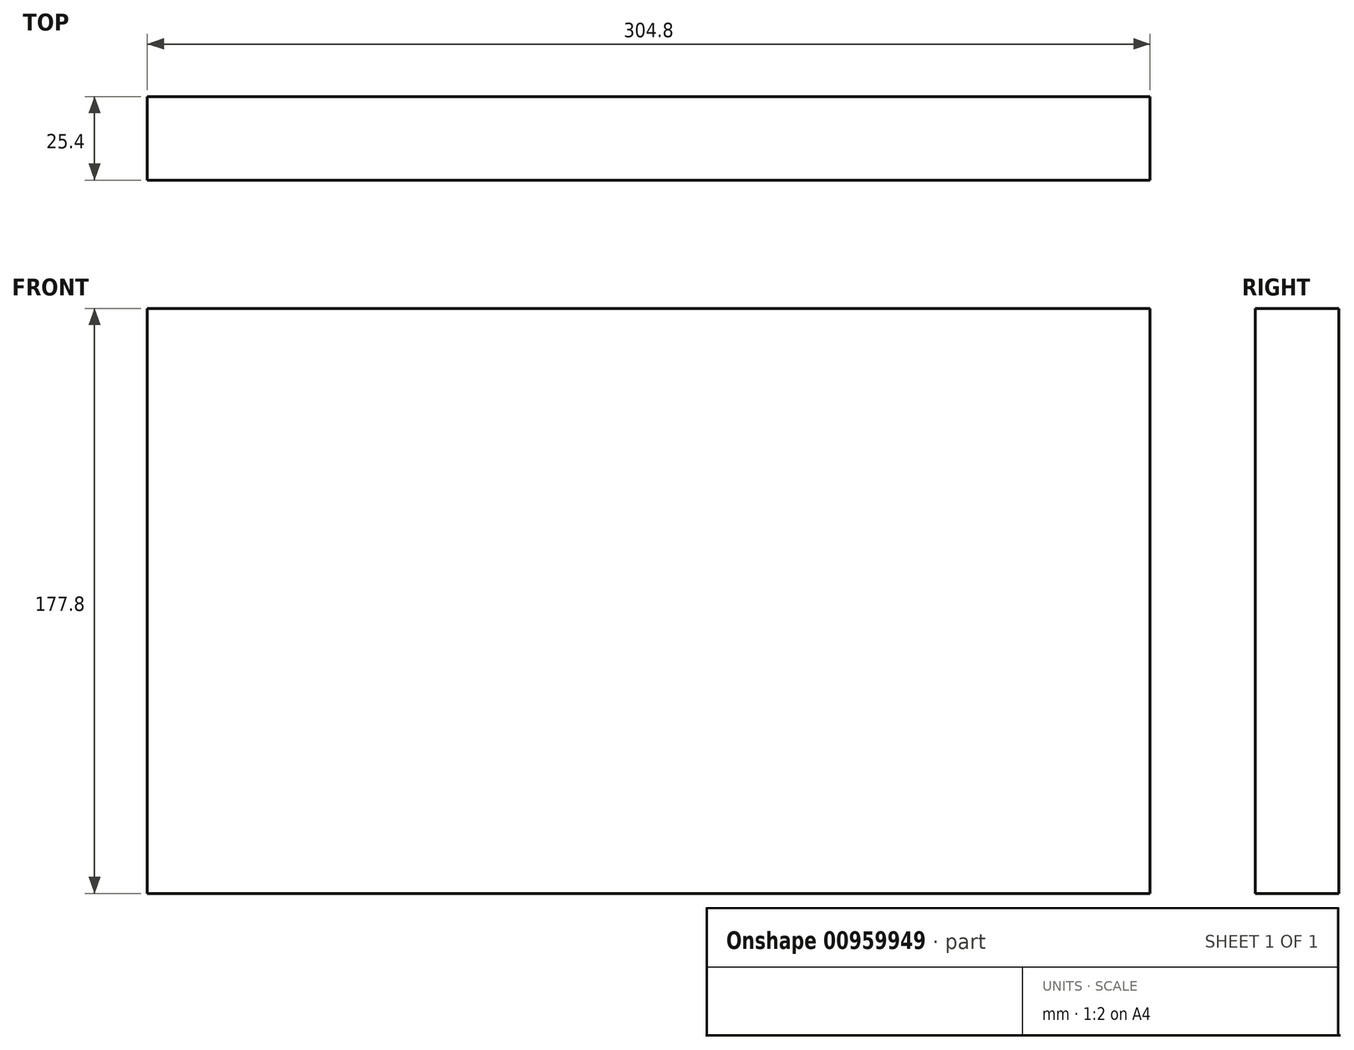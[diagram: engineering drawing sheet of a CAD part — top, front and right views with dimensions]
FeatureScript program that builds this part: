
annotation { "Feature Type Name" : "Feature", "Feature Type Description" : "" }
export const myFeature = defineFeature(function(context is Context, id is Id, definition is map)
    precondition{}
    {
        {
            var Q0;
            Q0=qCreatedBy(makeId("Front.planeOp"),FACE);
            var sketch = newSketch(context, id + "F0", { "sketchPlane" : qUnion([Q0])});
            skLineSegment(sketch, "E0.bottom", {"start": v(-88.9, -88.9) * mm, "end": v(88.9, -88.9) * mm});
            skLineSegment(sketch, "E0.top", {"start": v(-88.9, 88.9) * mm, "end": v(88.9, 88.9) * mm});
            skLineSegment(sketch, "E0.left", {"start": v(-88.9, -88.9) * mm, "end": v(-88.9, 88.9) * mm});
            skLineSegment(sketch, "E0.right", {"start": v(88.9, -88.9) * mm, "end": v(88.9, 88.9) * mm});
            skPoint(sketch, "E0.middle", {"position": v(0, 0) * mm});
            skLineSegment(sketch, "E1", {"start": v(-88.9, 88.9) * mm, "end": v(-215.9, 88.9) * mm});
            skLineSegment(sketch, "E2", {"start": v(-215.9, 88.9) * mm, "end": v(-215.9, -88.9) * mm});
            skLineSegment(sketch, "E3", {"start": v(-215.9, -88.9) * mm, "end": v(-88.9, -88.9) * mm});
            skSolve(sketch);
        }
        {
            var Q0;
            Q0 = qSketchRegion(id + "F0", true);
            extrude(context, id + "F1", {"entities" : qUnion([Q0]), "endBound" : BoundingType.SYMMETRIC, "depth" : 25.4 * mm, "offsetDistance" : 25.4 * mm});
        }
    });
